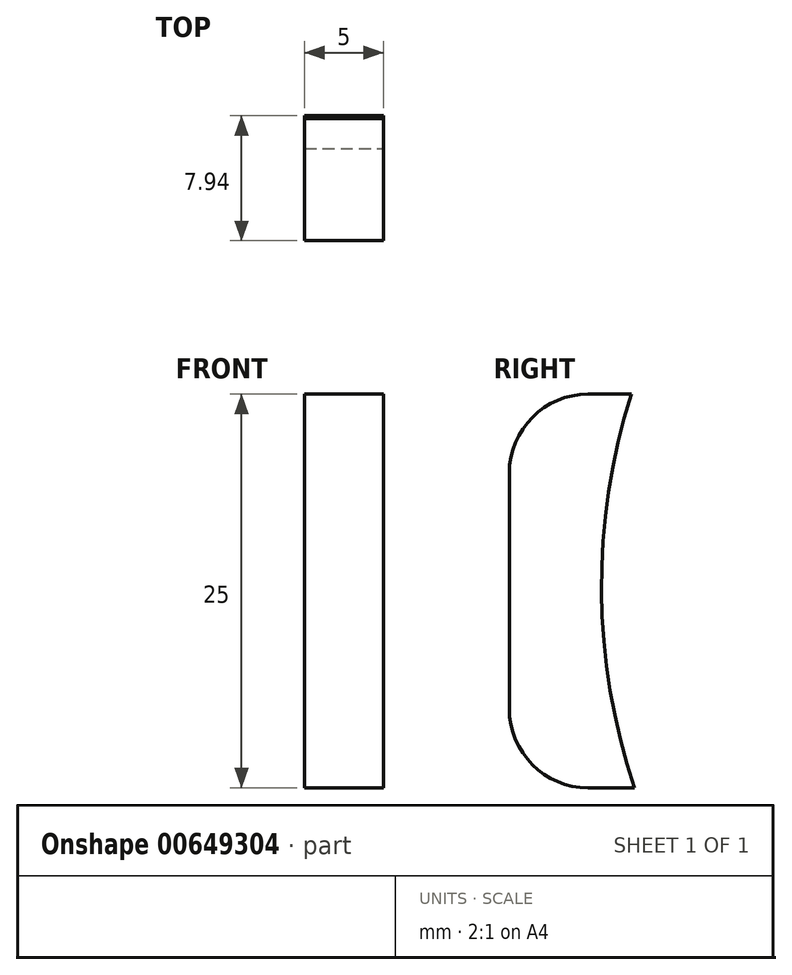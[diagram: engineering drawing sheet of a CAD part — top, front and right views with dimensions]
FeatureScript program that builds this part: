
annotation { "Feature Type Name" : "Feature", "Feature Type Description" : "" }
export const myFeature = defineFeature(function(context is Context, id is Id, definition is map)
    precondition{}
    {
        {
            var Q0;
            Q0=qCreatedBy(makeId("Top.planeOp"),FACE);
            var sketch = newSketch(context, id + "F0", { "sketchPlane" : qUnion([Q0])});
            skLineSegment(sketch, "E0.bottom", {"start": v(-6.03, 7.88) * mm, "end": v(-11.03, 7.88) * mm});
            skLineSegment(sketch, "E0.top", {"start": v(-6.03, 15.88) * mm, "end": v(-11.03, 15.88) * mm});
            skLineSegment(sketch, "E0.left", {"start": v(-6.03, 7.88) * mm, "end": v(-6.03, 15.88) * mm});
            skLineSegment(sketch, "E0.right", {"start": v(-11.03, 7.88) * mm, "end": v(-11.03, 15.88) * mm});
            skPoint(sketch, "E0.middle", {"position": v(-8.53, 11.88) * mm});
            skSolve(sketch);
        }
        {
            var Q0;
            Q0 = qSketchRegion(id + "F0", true);
            extrude(context, id + "F1", {"entities" : qUnion([Q0]), "depth" : 25 * mm, "offsetDistance" : 25 * mm});
        }
        {
            var Q0;
            Q0=qCreatedBy(makeId("Right.planeOp"),FACE);
            var sketch = newSketch(context, id + "F2", { "sketchPlane" : qUnion([Q0])});
            skCircle(sketch, "E1", {"center": v(53.98, 12.8) * mm, "radius": 40.25 * mm});
            skSolve(sketch);
        }
        {
            var Q0;
            Q0=sQuery(id+"F2.wireOp",VERTEX,"E1.center");
            var Q1;
            Q1=makeQuery(id+"F1.opExtrude","SWEPT_BODY",BODY,{"disambiguationData":[OSD([sQuery(id+"F0.wireOp",EDGE,"E0.bottom"),sQuery(id+"F0.wireOp",EDGE,"E0.top"),sQuery(id+"F0.wireOp",EDGE,"E0.left"),sQuery(id+"F0.wireOp",EDGE,"E0.right")])]});
            hole(context, id + "F3", {"style" : HoleStyle.SIMPLE, "endStyle" : HoleEndStyle.THROUGH, "holeDiameter" : 80.5 * mm, "majorDiameter" : 5 * mm, "isTappedThrough" : true, "tappedDepth" : 12 * mm, "tapClearance" : 3, "locations" : qUnion([Q0]), "scope" : qUnion([Q1])});
        }
        {
            var Q0;
            Q0=makeQuery(id+"F1.opExtrude","CAP_EDGE",EDGE,{"disambiguationData":[OSD([sQuery(id+"F0.wireOp",EDGE,"E0.bottom")])],"isStart":true});
            var Q1;
            Q1=makeQuery(id+"F1.opExtrude","CAP_EDGE",EDGE,{"disambiguationData":[OSD([sQuery(id+"F0.wireOp",EDGE,"E0.bottom")])],"isStart":false});
            fillet(context, id + "F4", {"entities" : qUnion([Q0, Q1]), "radius" : 5 * mm, "tangentPropagation" : true, "allowEdgeOverflow" : false});
        }
    });
